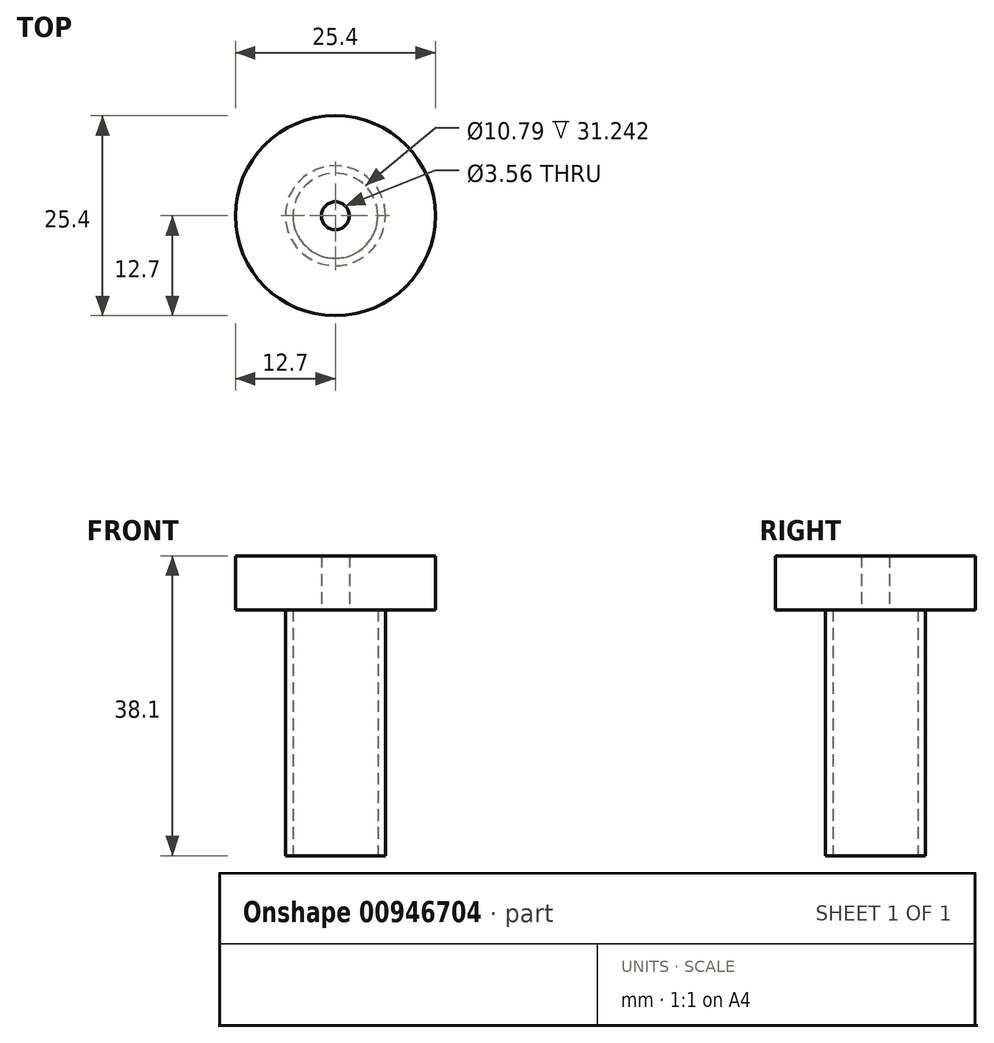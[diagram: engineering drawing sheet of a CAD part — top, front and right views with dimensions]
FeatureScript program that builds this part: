
annotation { "Feature Type Name" : "Feature", "Feature Type Description" : "" }
export const myFeature = defineFeature(function(context is Context, id is Id, definition is map)
    precondition{}
    {
        {
            var Q0;
            Q0=qCreatedBy(makeId("Top.planeOp"),FACE);
            var sketch = newSketch(context, id + "F0", { "sketchPlane" : qUnion([Q0])});
            skCircle(sketch, "E0", {"center": v(0, 0) * mm, "radius": 6.35 * mm});
            skSolve(sketch);
        }
        {
            var Q0;
            Q0 = qSketchRegion(id + "F0", true);
            extrude(context, id + "F1", {"entities" : qUnion([Q0]), "depth" : 38.1 * mm, "offsetDistance" : 25.4 * mm});
        }
        {
            var Q0;
            Q0=makeQuery(id+"F1.opExtrude","CAP_FACE",FACE,{"disambiguationData":[OSD([sQuery(id+"F0.wireOp",EDGE,"E0")])],"isStart":true});
            var sketch = newSketch(context, id + "F2", { "sketchPlane" : qUnion([Q0])});
            skCircle(sketch, "E1", {"center": v(0, 0) * mm, "radius": 1.78 * mm});
            skSolve(sketch);
        }
        {
            var Q0;
            Q0=makeQuery(id+"F1.opExtrude","CAP_FACE",FACE,{"disambiguationData":[OSD([sQuery(id+"F0.wireOp",EDGE,"E0")])],"isStart":true});
            var sketch = newSketch(context, id + "F3", { "sketchPlane" : qUnion([Q0])});
            skCircle(sketch, "E2", {"center": v(0, 0) * mm, "radius": 5.4 * mm});
            skSolve(sketch);
        }
        {
            var Q0;
            Q0 = qSketchRegion(id + "F3", true);
            extrude(context, id + "F4", {"entities" : qUnion([Q0]), "operationType" : NewBodyOperationType.REMOVE, "oppositeDirection" : true, "depth" : 32.5 * mm, "offsetDistance" : 25.4 * mm});
        }
        {
            var Q0;
            Q0=makeQuery(id+"F1.opExtrude","CAP_FACE",FACE,{"disambiguationData":[OSD([sQuery(id+"F0.wireOp",EDGE,"E0")])],"isStart":false});
            var sketch = newSketch(context, id + "F5", { "sketchPlane" : qUnion([Q0])});
            skCircle(sketch, "E3", {"center": v(0, 0) * mm, "radius": 12.7 * mm});
            skSolve(sketch);
        }
        {
            var Q0;
            Q0 = qSketchRegion(id + "F5", true);
            extrude(context, id + "F6", {"entities" : qUnion([Q0]), "operationType" : NewBodyOperationType.ADD, "oppositeDirection" : true, "depth" : 6.86 * mm, "offsetDistance" : 25.4 * mm});
        }
        {
            var Q0;
            Q0 = qSketchRegion(id + "F2", true);
            extrude(context, id + "F7", {"entities" : qUnion([Q0]), "operationType" : NewBodyOperationType.REMOVE, "oppositeDirection" : true, "depth" : 50.3 * mm, "offsetDistance" : 25.4 * mm});
        }
    });
